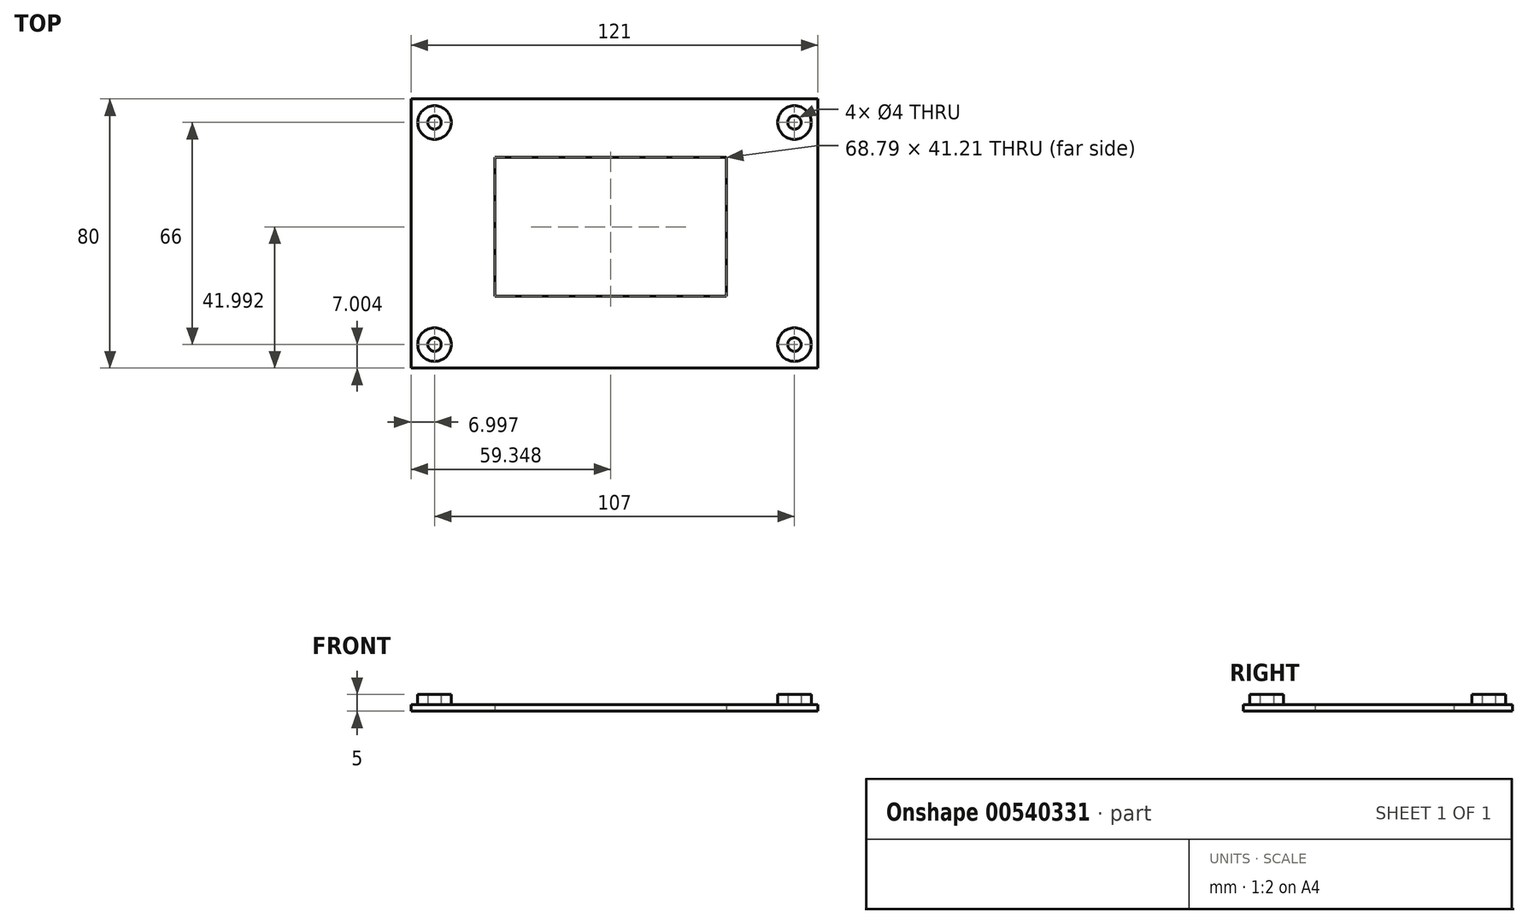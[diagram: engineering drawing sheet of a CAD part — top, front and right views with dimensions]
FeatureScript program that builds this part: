
annotation { "Feature Type Name" : "Feature", "Feature Type Description" : "" }
export const myFeature = defineFeature(function(context is Context, id is Id, definition is map)
    precondition{}
    {
        {
            var Q0;
            Q0=qCreatedBy(makeId("Top.planeOp"),FACE);
            var sketch = newSketch(context, id + "F0", { "sketchPlane" : qUnion([Q0])});
            skLineSegment(sketch, "E0.bottom", {"start": v(-66.04, 46.67) * mm, "end": v(54.96, 46.67) * mm});
            skLineSegment(sketch, "E0.top", {"start": v(-66.04, -33.33) * mm, "end": v(54.96, -33.33) * mm});
            skLineSegment(sketch, "E0.left", {"start": v(-66.04, 46.67) * mm, "end": v(-66.04, -33.33) * mm});
            skLineSegment(sketch, "E0.right", {"start": v(54.96, 46.67) * mm, "end": v(54.96, -33.33) * mm});
            skCircle(sketch, "E1", {"center": v(-59.04, 39.67) * mm, "radius": 2 * mm});
            skCircle(sketch, "E2", {"center": v(-59.04, 39.67) * mm, "radius": 5 * mm});
            skCircle(sketch, "E3", {"center": v(-59.04, -26.33) * mm, "radius": 2 * mm});
            skCircle(sketch, "E4", {"center": v(-59.04, -26.33) * mm, "radius": 5 * mm});
            skCircle(sketch, "E5", {"center": v(47.96, 39.67) * mm, "radius": 5 * mm});
            skCircle(sketch, "E6", {"center": v(47.96, 39.67) * mm, "radius": 2 * mm});
            skCircle(sketch, "E7", {"center": v(47.96, -26.33) * mm, "radius": 5 * mm});
            skCircle(sketch, "E8", {"center": v(47.96, -26.33) * mm, "radius": 2 * mm});
            skLineSegment(sketch, "E9.bottom", {"start": v(-41.09, -11.94) * mm, "end": v(27.7, -11.94) * mm});
            skLineSegment(sketch, "E9.top", {"start": v(-41.09, 29.27) * mm, "end": v(27.7, 29.27) * mm});
            skLineSegment(sketch, "E9.left", {"start": v(-41.09, -11.94) * mm, "end": v(-41.09, 29.27) * mm});
            skLineSegment(sketch, "E9.right", {"start": v(27.7, -11.94) * mm, "end": v(27.7, 29.27) * mm});
            skSolve(sketch);
        }
        {
            var Q0;
            Q0=makeQuery(id+"F0.imprint","IMPRINT",FACE,{"disambiguationData":[TD([[makeQuery(id+"F0.imprint","IMPRINT",EDGE,{"derivedFrom":sQuery(id+"F0.wireOp",EDGE,"E0.bottom")}),-1.0]])]});
            extrude(context, id + "F1", {"entities" : qUnion([Q0]), "depth" : 2 * mm, "offsetDistance" : 25 * mm});
        }
        {
            var Q0;
            Q0=makeQuery(id+"F0.imprint","IMPRINT",FACE,{"disambiguationData":[TD([[makeQuery(id+"F0.imprint","IMPRINT",EDGE,{"derivedFrom":sQuery(id+"F0.wireOp",EDGE,"E1")}),-1.0]])]});
            var Q1;
            Q1=makeQuery(id+"F0.imprint","IMPRINT",FACE,{"disambiguationData":[TD([[makeQuery(id+"F0.imprint","IMPRINT",EDGE,{"derivedFrom":sQuery(id+"F0.wireOp",EDGE,"E5")}),1.0]])]});
            var Q2;
            Q2=makeQuery(id+"F0.imprint","IMPRINT",FACE,{"disambiguationData":[TD([[makeQuery(id+"F0.imprint","IMPRINT",EDGE,{"derivedFrom":sQuery(id+"F0.wireOp",EDGE,"E7")}),1.0]])]});
            var Q3;
            Q3=makeQuery(id+"F0.imprint","IMPRINT",FACE,{"disambiguationData":[TD([[makeQuery(id+"F0.imprint","IMPRINT",EDGE,{"derivedFrom":sQuery(id+"F0.wireOp",EDGE,"E3")}),-1.0]])]});
            extrude(context, id + "F2", {"entities" : qUnion([Q0, Q1, Q2, Q3]), "operationType" : NewBodyOperationType.ADD, "depth" : 5 * mm, "offsetDistance" : 25 * mm});
        }
    });
